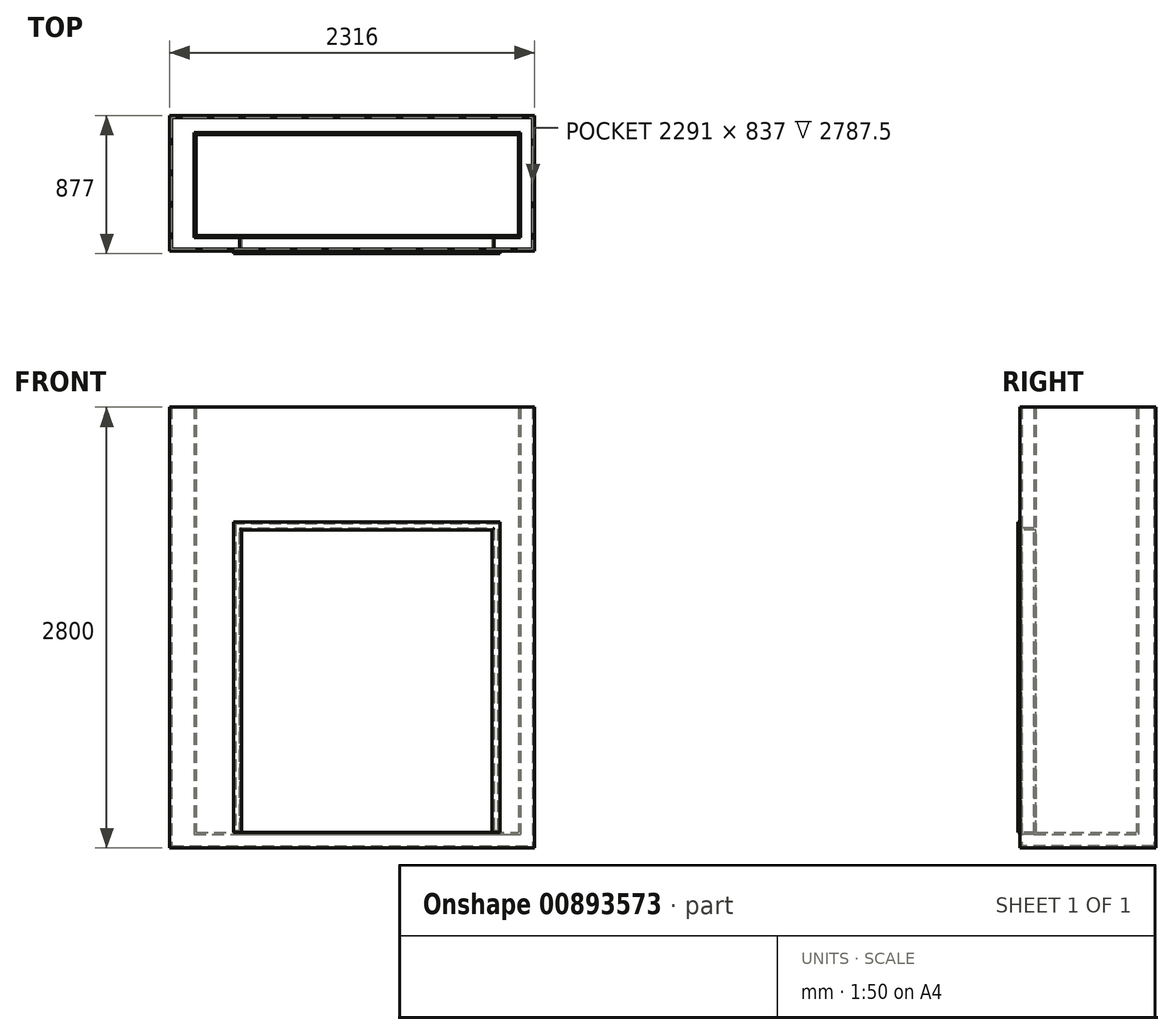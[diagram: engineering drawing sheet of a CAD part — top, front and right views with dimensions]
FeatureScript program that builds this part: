
annotation { "Feature Type Name" : "Feature", "Feature Type Description" : "" }
export const myFeature = defineFeature(function(context is Context, id is Id, definition is map)
    precondition{}
    {
        {
            var Q0;
            Q0=qCreatedBy(makeId("Top.planeOp"),FACE);
            var sketch = newSketch(context, id + "F0", { "sketchPlane" : qUnion([Q0])});
            skLineSegment(sketch, "E0.bottom", {"start": v(0, 0) * mm, "end": v(2048, 0) * mm});
            skLineSegment(sketch, "E0.top", {"start": v(0, 640) * mm, "end": v(2048, 640) * mm});
            skLineSegment(sketch, "E0.left", {"start": v(0, 0) * mm, "end": v(0, 640) * mm});
            skLineSegment(sketch, "E0.right", {"start": v(2048, 0) * mm, "end": v(2048, 640) * mm});
            skSolve(sketch);
        }
        {
            var Q0;
            Q0 = qSketchRegion(id + "F0", true);
            extrude(context, id + "F1", {"entities" : qUnion([Q0]), "oppositeDirection" : true, "depth" : 100 * mm, "offsetDistance" : 25 * mm});
        }
        {
            var Q0;
            Q0=qCreatedBy(makeId("Top.planeOp"),FACE);
            var sketch = newSketch(context, id + "F2", { "sketchPlane" : qUnion([Q0])});
            skLineSegment(sketch, "E1", {"start": v(0, 0) * mm, "end": v(0, 640) * mm});
            skLineSegment(sketch, "E2", {"start": v(0, 640) * mm, "end": v(2048, 640) * mm});
            skLineSegment(sketch, "E3", {"start": v(2048, 640) * mm, "end": v(2048, 0) * mm});
            skLineSegment(sketch, "E4.0", {"start": v(2148, 762) * mm, "end": v(2148, -100) * mm});
            skLineSegment(sketch, "E5.0", {"start": v(-168, 762) * mm, "end": v(2148, 762) * mm});
            skLineSegment(sketch, "E6.0", {"start": v(-168, -100) * mm, "end": v(-168, 762) * mm});
            skLineSegment(sketch, "E7", {"start": v(0, 0) * mm, "end": v(2048, 0) * mm});
            skLineSegment(sketch, "E8.0", {"start": v(-168, -100) * mm, "end": v(2148, -100) * mm});
            skSolve(sketch);
        }
        {
            var Q0;
            Q0 = qSketchRegion(id + "F2", true);
            extrude(context, id + "F3", {"entities" : qUnion([Q0]), "operationType" : NewBodyOperationType.ADD, "depth" : 2700 * mm, "offsetDistance" : 25 * mm, "hasSecondDirection" : true, "secondDirectionOppositeDirection" : true, "secondDirectionDepth" : 100 * mm});
        }
        {
            var Q0;
            Q0=makeQuery(id+"F3.opExtrude","SWEPT_FACE",FACE,{"disambiguationData":[OSD([sQuery(id+"F2.wireOp",EDGE,"E8.0")])]});
            var sketch = newSketch(context, id + "F4", { "sketchPlane" : qUnion([Q0])});
            skLineSegment(sketch, "E9", {"start": v(288.1, 0) * mm, "end": v(288.1, 1920) * mm});
            skLineSegment(sketch, "E10", {"start": v(288.1, 1920) * mm, "end": v(1880.1, 1920) * mm});
            skLineSegment(sketch, "E11", {"start": v(1880.1, 1920) * mm, "end": v(1880.1, 0) * mm});
            skLineSegment(sketch, "E12", {"start": v(288.1, 0) * mm, "end": v(1880.1, 0) * mm});
            skSolve(sketch);
        }
        {
            var Q0;
            Q0 = qSketchRegion(id + "F4", true);
            extrude(context, id + "F5", {"entities" : qUnion([Q0]), "operationType" : NewBodyOperationType.REMOVE, "oppositeDirection" : true, "depth" : 100 * mm, "offsetDistance" : 25 * mm});
        }
        {
            var Q0;
            Q0=makeQuery(id+"F3.opExtrude","SWEPT_FACE",FACE,{"disambiguationData":[OSD([sQuery(id+"F2.wireOp",EDGE,"E8.0")])]});
            var sketch = newSketch(context, id + "F6", { "sketchPlane" : qUnion([Q0])});
            skLineSegment(sketch, "E13", {"start": v(288.1, 0) * mm, "end": v(288.1, 1920) * mm});
            skLineSegment(sketch, "E14", {"start": v(288.1, 1920) * mm, "end": v(1880.1, 1920) * mm});
            skLineSegment(sketch, "E15", {"start": v(1880.1, 1920) * mm, "end": v(1880.1, 0) * mm});
            skLineSegment(sketch, "E16", {"start": v(1880.1, 0) * mm, "end": v(1930.1, 0) * mm});
            skLineSegment(sketch, "E17", {"start": v(1930.1, 0) * mm, "end": v(1930.1, 1970) * mm});
            skLineSegment(sketch, "E18", {"start": v(1930.1, 1970) * mm, "end": v(238.1, 1970) * mm});
            skLineSegment(sketch, "E19", {"start": v(238.1, 1970) * mm, "end": v(238.1, 0) * mm});
            skLineSegment(sketch, "E20", {"start": v(238.1, 0) * mm, "end": v(288.1, 0) * mm});
            skSolve(sketch);
        }
        {
            var Q0;
            Q0 = qSketchRegion(id + "F6", true);
            extrude(context, id + "F7", {"entities" : qUnion([Q0]), "operationType" : NewBodyOperationType.ADD, "depth" : 15 * mm, "offsetDistance" : 25 * mm});
        }
        {
            var Q0;
            Q0=makeQuery(id+"F7.opExtrude","CAP_EDGE",EDGE,{"disambiguationData":[OSD([sQuery(id+"F6.wireOp",EDGE,"E13")])],"isStart":false});
            var Q1;
            Q1=makeQuery(id+"F7.opExtrude","CAP_EDGE",EDGE,{"disambiguationData":[OSD([sQuery(id+"F6.wireOp",EDGE,"E14")])],"isStart":false});
            var Q2;
            Q2=makeQuery(id+"F7.opExtrude","CAP_EDGE",EDGE,{"disambiguationData":[OSD([sQuery(id+"F6.wireOp",EDGE,"E15")])],"isStart":false});
            fillet(context, id + "F8", {"entities" : qUnion([Q0, Q1, Q2]), "radius" : 10 * mm, "tangentPropagation" : true, "allowEdgeOverflow" : false});
        }
        {
            var Q0;
            Q0=makeQuery(id+"F3.opExtrude","CAP_FACE",FACE,{"disambiguationData":[OSD([sQuery(id+"F2.wireOp",EDGE,"E1"),sQuery(id+"F2.wireOp",EDGE,"E2"),sQuery(id+"F2.wireOp",EDGE,"E3"),sQuery(id+"F2.wireOp",EDGE,"E4.0"),sQuery(id+"F2.wireOp",EDGE,"E5.0"),sQuery(id+"F2.wireOp",EDGE,"E6.0"),sQuery(id+"F2.wireOp",EDGE,"E7"),sQuery(id+"F2.wireOp",EDGE,"E8.0")])],"isStart":false});
            shell(context, id + "F9", {"entities" : qUnion([Q0]), "thickness" : 12.5 * mm});
        }
    });
